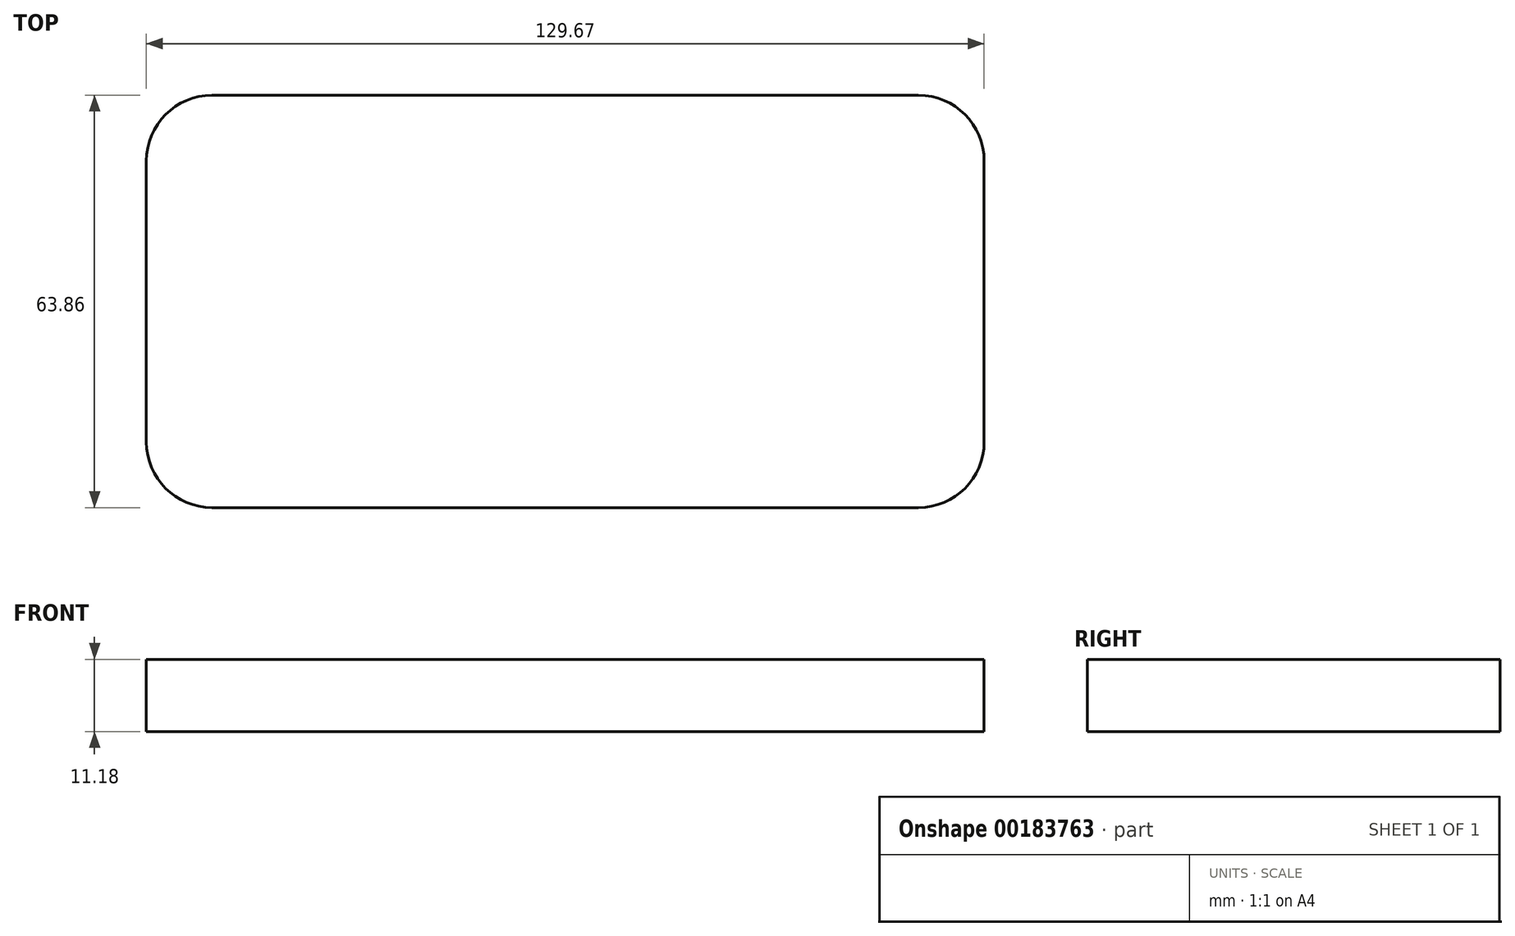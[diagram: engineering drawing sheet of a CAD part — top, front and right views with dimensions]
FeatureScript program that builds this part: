
annotation { "Feature Type Name" : "Feature", "Feature Type Description" : "" }
export const myFeature = defineFeature(function(context is Context, id is Id, definition is map)
    precondition{}
    {
        {
            var Q0;
            Q0=qCreatedBy(makeId("Top.planeOp"),FACE);
            var sketch = newSketch(context, id + "F0", { "sketchPlane" : qUnion([Q0])});
            skLineSegment(sketch, "E0.bottom", {"start": v(54.2, -37.45) * mm, "end": v(-55.14, -37.45) * mm});
            skLineSegment(sketch, "E0.top", {"start": v(54.2, 26.4) * mm, "end": v(-55.14, 26.4) * mm});
            skLineSegment(sketch, "E0.left", {"start": v(64.37, -27.29) * mm, "end": v(64.37, 16.25) * mm});
            skLineSegment(sketch, "E0.right", {"start": v(-65.3, -27.29) * mm, "end": v(-65.3, 16.25) * mm});
            skPoint(sketch, "E0.middle", {"position": v(-0.47, -5.52) * mm});
            skPoint(sketch, "E1.visualSharp", {"position": v(-65.3, 26.4) * mm});
            skArc(sketch, "E1.filletArc", {"start": v(-55.14, 26.4) * mm, "mid": v(-62.32, 23.43) * mm, "end": v(-65.3, 16.25) * mm});
            skPoint(sketch, "E2.visualSharp", {"position": v(64.37, 26.4) * mm});
            skArc(sketch, "E2.filletArc", {"start": v(64.37, 16.25) * mm, "mid": v(61.4, 23.43) * mm, "end": v(54.2, 26.4) * mm});
            skPoint(sketch, "E3.visualSharp", {"position": v(64.37, -37.45) * mm});
            skArc(sketch, "E3.filletArc", {"start": v(54.2, -37.45) * mm, "mid": v(61.4, -34.47) * mm, "end": v(64.37, -27.29) * mm});
            skPoint(sketch, "E4.visualSharp", {"position": v(-65.3, -37.45) * mm});
            skArc(sketch, "E4.filletArc", {"start": v(-65.3, -27.29) * mm, "mid": v(-62.32, -34.47) * mm, "end": v(-55.14, -37.45) * mm});
            skSolve(sketch);
        }
        {
            var Q0;
            Q0=makeQuery(id+"F0.imprint","IMPRINT",FACE,{"disambiguationData":[TD([[makeQuery(id+"F0.imprint","IMPRINT",EDGE,{"derivedFrom":sQuery(id+"F0.wireOp",EDGE,"E0.bottom")}),-1.0]])]});
            extrude(context, id + "F1", {"entities" : qUnion([Q0]), "depth" : 11.18 * mm});
        }
    });
